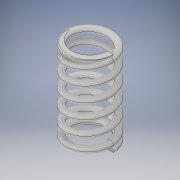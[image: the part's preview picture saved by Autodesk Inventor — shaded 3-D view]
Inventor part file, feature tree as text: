
AUTODESK INVENTOR PART (.ipt)
format: ipt  version: 2018 (Build 220112000, 112)  size: 722,432 bytes
history: native  units: in
note: dims shown in document units (in); Inventor stores cm internally (conversion verified against a paired STEP export)
features: extrude x1
ambient origin geometry x8: Origin, YZ Plane, XZ Plane, XY Plane, X Axis, Y Axis, Z Axis, Center Point
bodies: Solid1 (feature_tree)
feature tree (1):
  extrude  "Extrude1"  [1 undecoded]
note: 1 required parameter value undecoded (feature->parameter linkage not recoverable at this tier; creation-order binding heuristic only, values carry confidence <= 0.55)
